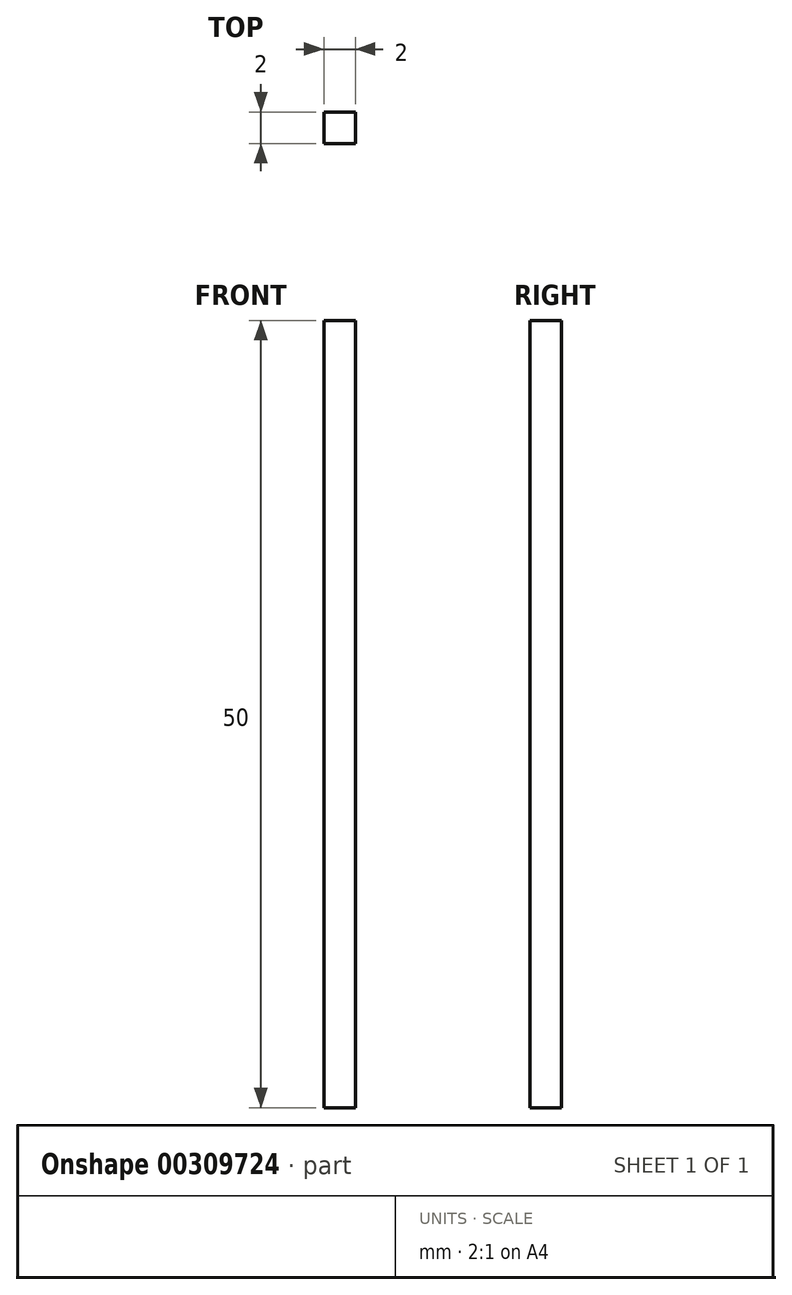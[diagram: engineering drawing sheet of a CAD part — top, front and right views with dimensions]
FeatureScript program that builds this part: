
annotation { "Feature Type Name" : "Feature", "Feature Type Description" : "" }
export const myFeature = defineFeature(function(context is Context, id is Id, definition is map)
    precondition{}
    {
        {
            var Q0;
            Q0=qCreatedBy(makeId("Front.planeOp"),FACE);
            var sketch = newSketch(context, id + "F0", { "sketchPlane" : qUnion([Q0])});
            skLineSegment(sketch, "E0", {"start": v(0, 0) * mm, "end": v(0, 50) * mm});
            skLineSegment(sketch, "E1", {"start": v(0, 50) * mm, "end": v(2, 50) * mm});
            skLineSegment(sketch, "E2", {"start": v(2, 50) * mm, "end": v(2, 0) * mm});
            skLineSegment(sketch, "E3", {"start": v(2, 0) * mm, "end": v(0, 0) * mm});
            skSolve(sketch);
        }
        {
            var Q0;
            Q0=makeQuery(id+"F0.imprint","IMPRINT",FACE,{"disambiguationData":[TD([[makeQuery(id+"F0.imprint","IMPRINT",EDGE,{"derivedFrom":sQuery(id+"F0.wireOp",EDGE,"E0")}),-1.0]])]});
            extrude(context, id + "F1", {"entities" : qUnion([Q0]), "depth" : 2 * mm});
        }
    });
